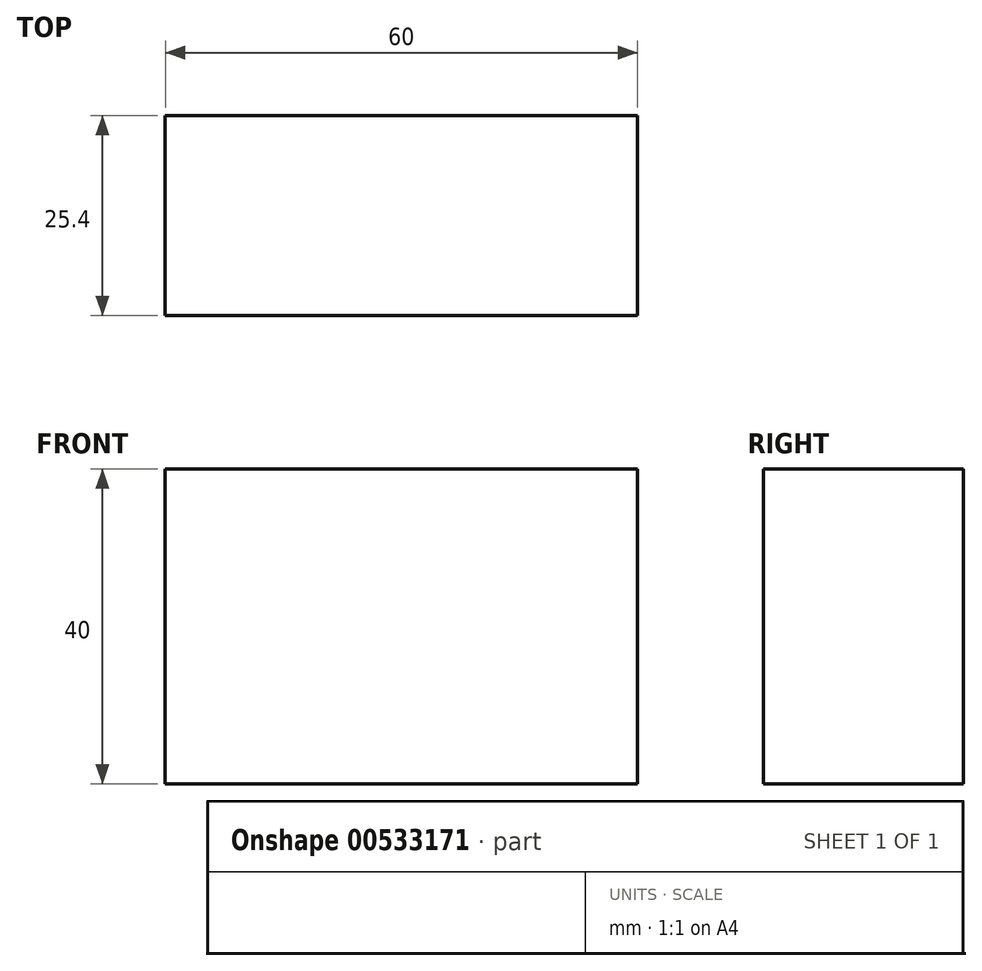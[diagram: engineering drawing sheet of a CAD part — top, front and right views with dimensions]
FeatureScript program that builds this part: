
annotation { "Feature Type Name" : "Feature", "Feature Type Description" : "" }
export const myFeature = defineFeature(function(context is Context, id is Id, definition is map)
    precondition{}
    {
        {
            var Q0;
            Q0=qCreatedBy(makeId("Front.planeOp"),FACE);
            var sketch = newSketch(context, id + "F0", { "sketchPlane" : qUnion([Q0])});
            skLineSegment(sketch, "E0.bottom", {"start": v(-37.55, 20.76) * mm, "end": v(22.45, 20.76) * mm});
            skLineSegment(sketch, "E0.top", {"start": v(-37.55, -19.24) * mm, "end": v(22.45, -19.24) * mm});
            skLineSegment(sketch, "E0.left", {"start": v(-37.55, 20.76) * mm, "end": v(-37.55, -19.24) * mm});
            skLineSegment(sketch, "E0.right", {"start": v(22.45, 20.76) * mm, "end": v(22.45, -19.24) * mm});
            skSolve(sketch);
        }
        {
            var Q0;
            Q0 = qSketchRegion(id + "F0", true);
            extrude(context, id + "F1", {"entities" : qUnion([Q0]), "depth" : 25.4 * mm, "offsetDistance" : 25.4 * mm});
        }
    });
